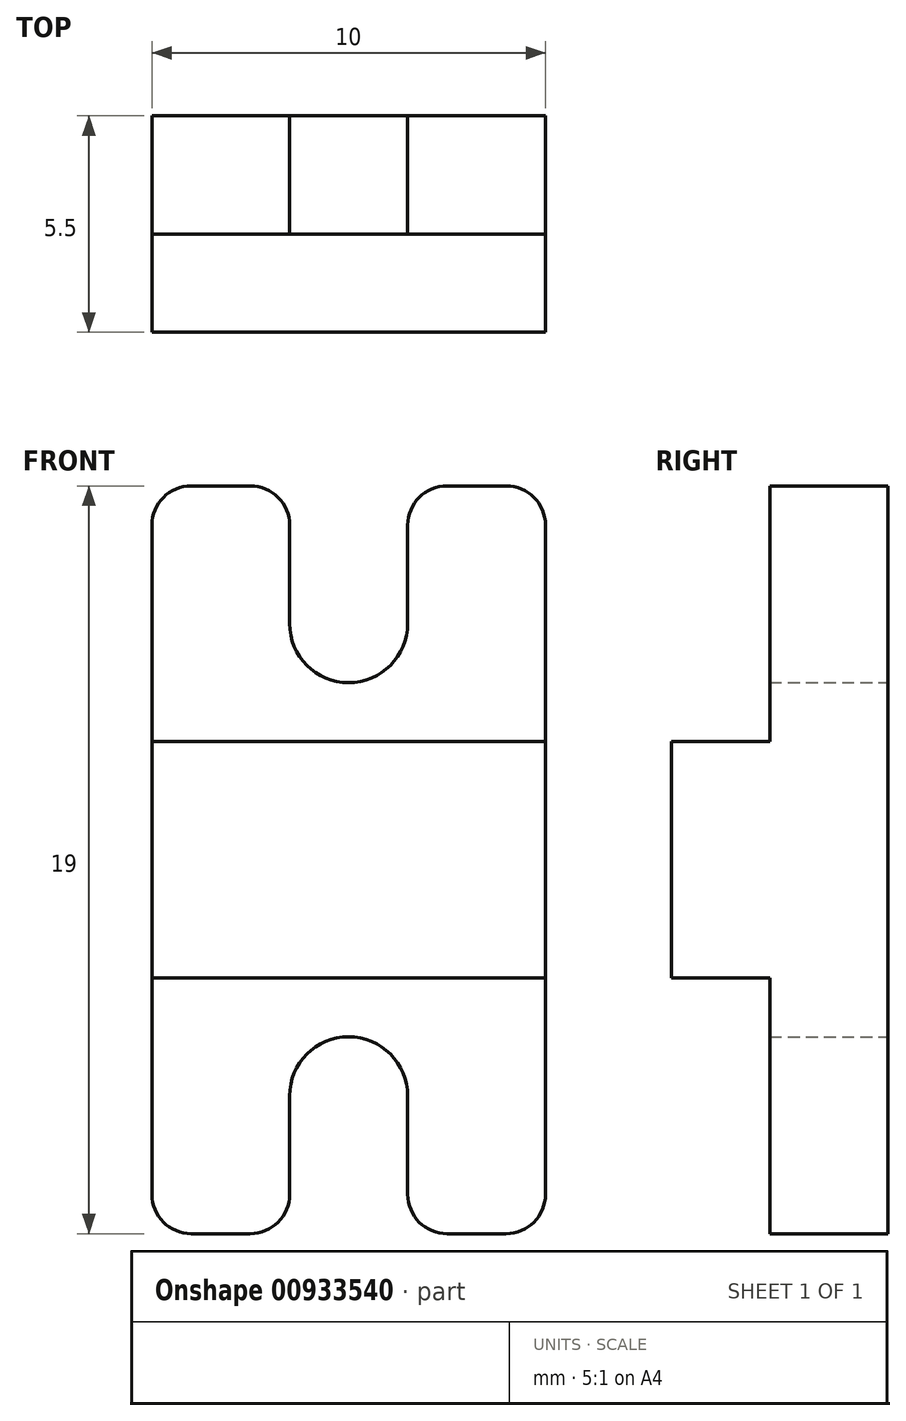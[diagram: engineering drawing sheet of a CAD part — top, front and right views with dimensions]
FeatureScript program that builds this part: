
annotation { "Feature Type Name" : "Feature", "Feature Type Description" : "" }
export const myFeature = defineFeature(function(context is Context, id is Id, definition is map)
    precondition{}
    {
        {
            var Q0;
            Q0=qCreatedBy(makeId("Front.planeOp"),FACE);
            var sketch = newSketch(context, id + "F0", { "sketchPlane" : qUnion([Q0])});
            skLineSegment(sketch, "E0.bottom", {"start": v(1, 0) * mm, "end": v(2.5, 0) * mm});
            skLineSegment(sketch, "E0.top", {"start": v(1, 19) * mm, "end": v(2.5, 19) * mm});
            skLineSegment(sketch, "E0.left", {"start": v(0, 1) * mm, "end": v(0, 18) * mm});
            skLineSegment(sketch, "E0.right", {"start": v(10, 1) * mm, "end": v(10, 18) * mm});
            skPoint(sketch, "E1.visualSharp", {"position": v(0, 19) * mm});
            skArc(sketch, "E1.filletArc", {"start": v(1, 19) * mm, "mid": v(0.3, 18.7) * mm, "end": v(0, 18) * mm});
            skPoint(sketch, "E2.visualSharp", {"position": v(10, 19) * mm});
            skArc(sketch, "E2.filletArc", {"start": v(10, 18) * mm, "mid": v(9.7, 18.7) * mm, "end": v(9, 19) * mm});
            skPoint(sketch, "E3.visualSharp", {"position": v(10, 0) * mm});
            skArc(sketch, "E3.filletArc", {"start": v(9, 0) * mm, "mid": v(9.7, 0.3) * mm, "end": v(10, 1) * mm});
            skPoint(sketch, "E4.visualSharp", {"position": v(0, 0) * mm});
            skArc(sketch, "E4.filletArc", {"start": v(0, 1) * mm, "mid": v(0.3, 0.3) * mm, "end": v(1, 0) * mm});
            skLineSegment(sketch, "E5", {"start": v(0, 9.5) * mm, "end": v(10, 9.5) * mm, "construction": true});
            skLineSegment(sketch, "E6", {"start": v(0, 9.5) * mm, "end": v(0, 6.5) * mm, "construction": true});
            skLineSegment(sketch, "E7.bottom", {"start": v(0, 6.5) * mm, "end": v(10, 6.5) * mm});
            skLineSegment(sketch, "E7.top", {"start": v(0, 12.5) * mm, "end": v(10, 12.5) * mm});
            skLineSegment(sketch, "E7.left", {"start": v(0, 6.5) * mm, "end": v(0, 12.5) * mm});
            skLineSegment(sketch, "E7.right", {"start": v(10, 6.5) * mm, "end": v(10, 12.5) * mm});
            skLineSegment(sketch, "E8", {"start": v(5, 9.5) * mm, "end": v(5, 15.5) * mm, "construction": true});
            skLineSegment(sketch, "E9", {"start": v(5, 9.5) * mm, "end": v(5, 3.5) * mm, "construction": true});
            skArc(sketch, "E10", {"start": v(3.5, 15.5) * mm, "mid": v(5, 14) * mm, "end": v(6.5, 15.5) * mm});
            skArc(sketch, "E11", {"start": v(6.5, 3.5) * mm, "mid": v(5, 5) * mm, "end": v(3.5, 3.5) * mm});
            skLineSegment(sketch, "E12", {"start": v(6.5, 15.5) * mm, "end": v(6.5, 18) * mm});
            skLineSegment(sketch, "E13", {"start": v(3.5, 3.5) * mm, "end": v(3.5, 1) * mm});
            skLineSegment(sketch, "E14", {"start": v(3.5, 15.5) * mm, "end": v(3.5, 18) * mm});
            skLineSegment(sketch, "E15", {"start": v(6.5, 3.5) * mm, "end": v(6.5, 1) * mm});
            skLineSegment(sketch, "E16.trimOffspring", {"start": v(7.5, 19) * mm, "end": v(9, 19) * mm});
            skLineSegment(sketch, "E17.trimOffspring", {"start": v(7.5, 0) * mm, "end": v(9, 0) * mm});
            skPoint(sketch, "E18.visualSharp", {"position": v(3.5, 19) * mm});
            skArc(sketch, "E18.filletArc", {"start": v(3.5, 18) * mm, "mid": v(3.2, 18.7) * mm, "end": v(2.5, 19) * mm});
            skPoint(sketch, "E19.visualSharp", {"position": v(6.5, 19) * mm});
            skArc(sketch, "E19.filletArc", {"start": v(7.5, 19) * mm, "mid": v(6.8, 18.7) * mm, "end": v(6.5, 18) * mm});
            skPoint(sketch, "E20.visualSharp", {"position": v(6.5, 0) * mm});
            skArc(sketch, "E20.filletArc", {"start": v(6.5, 1) * mm, "mid": v(6.8, 0.3) * mm, "end": v(7.5, 0) * mm});
            skPoint(sketch, "E21.visualSharp", {"position": v(3.5, 0) * mm});
            skArc(sketch, "E21.filletArc", {"start": v(2.5, 0) * mm, "mid": v(3.2, 0.3) * mm, "end": v(3.5, 1) * mm});
            skSolve(sketch);
        }
        {
            var Q0;
            {var subQ0=sQuery(id+"F0.wireOp",EDGE,"E7.bottom");Q0=makeQuery(id+"F0.imprint","IMPRINT",FACE,{"disambiguationData":[TD([[makeQuery(id+"F0.imprint","IMPRINT",EDGE,{"derivedFrom":subQ0}),1.0]])]});}
            extrude(context, id + "F1", {"entities" : qUnion([Q0]), "depth" : 5.5 * mm, "offsetDistance" : 25 * mm});
        }
        {
            var Q0;
            Q0=makeQuery(id+"F0.imprint","IMPRINT",FACE,{"disambiguationData":[TD([[makeQuery(id+"F0.imprint","IMPRINT",EDGE,{"derivedFrom":sQuery(id+"F0.wireOp",EDGE,"E0.top")}),-1.0]])]});
            var Q1;
            Q1=makeQuery(id+"F0.imprint","IMPRINT",FACE,{"disambiguationData":[TD([[makeQuery(id+"F0.imprint","IMPRINT",EDGE,{"derivedFrom":sQuery(id+"F0.wireOp",EDGE,"E0.bottom")}),1.0]])]});
            extrude(context, id + "F2", {"entities" : qUnion([Q0, Q1]), "operationType" : NewBodyOperationType.ADD, "depth" : 3 * mm, "offsetDistance" : 25 * mm});
        }
    });
